# Revit family: QF_HOSHIZAKI_KMD-270ABE-R452
name_source: partatom
category: Specialty Equipment
revit_build: Autodesk Revit 2016 (Build: 20150220_1215(x64)
units: mm (PartAtom-declared; Revit-internal decimal feet)

## family parameters
Always vertical = Yes
Cut with Voids When Loaded = No
OmniClass Number = 23.40.40.14
OmniClass Title = Food Service Equipment
Part Type = Normal
Room Calculation Point = No
Round Connector Dimension = Use Diameter
Shared = No
Work Plane-Based = No

## types (1)
- KMD-270ABE-R452_230V/1Ph/50Hz
    Accessory = No
    Apparent Power = 984 VA
    Assembly Code = E1090320
    Cold Water Flow = 0.0 L/s
    Cold Water Size = 13 mm
    Cold Water Temperature Recommended = 0 °C
    Conn Conduit = No
    Cost = 0 $
    Cycle = 50 Hz
    Depth Actual = 625 mm  [stored 2.05052 ft]
    Description = MODULAR KM ICE MAKER, 275KG PER 24 HOURS, CRESCENT
    Electric power = 984 W
    FL Amps = 4 A
    Height Actual = 610 mm  [stored 2.00131 ft]
    Indirect Waste Size = 19 mm
    Length Actual = 560 mm  [stored 1.83727 ft]
    Manufacturer = HOSHIZAKI
    Max Overcurrent Protection = 0 A
    Min Ckt Ampacity = 0 A
    Model = KMD-270ABE-R452
    Number of Poles = 2
    Phase = 1
    URL = www.hoshizaki-europe.com
    Volts = 230 V
    Weight = 57.00 kg

note: [stored X ft] marks values corroborated as IEEE doubles in the binary element streams (Revit-internal decimal feet)

## geometry (parser evidence)
native form markers: Sweep x5
no freeform markers — native parametric forms only
